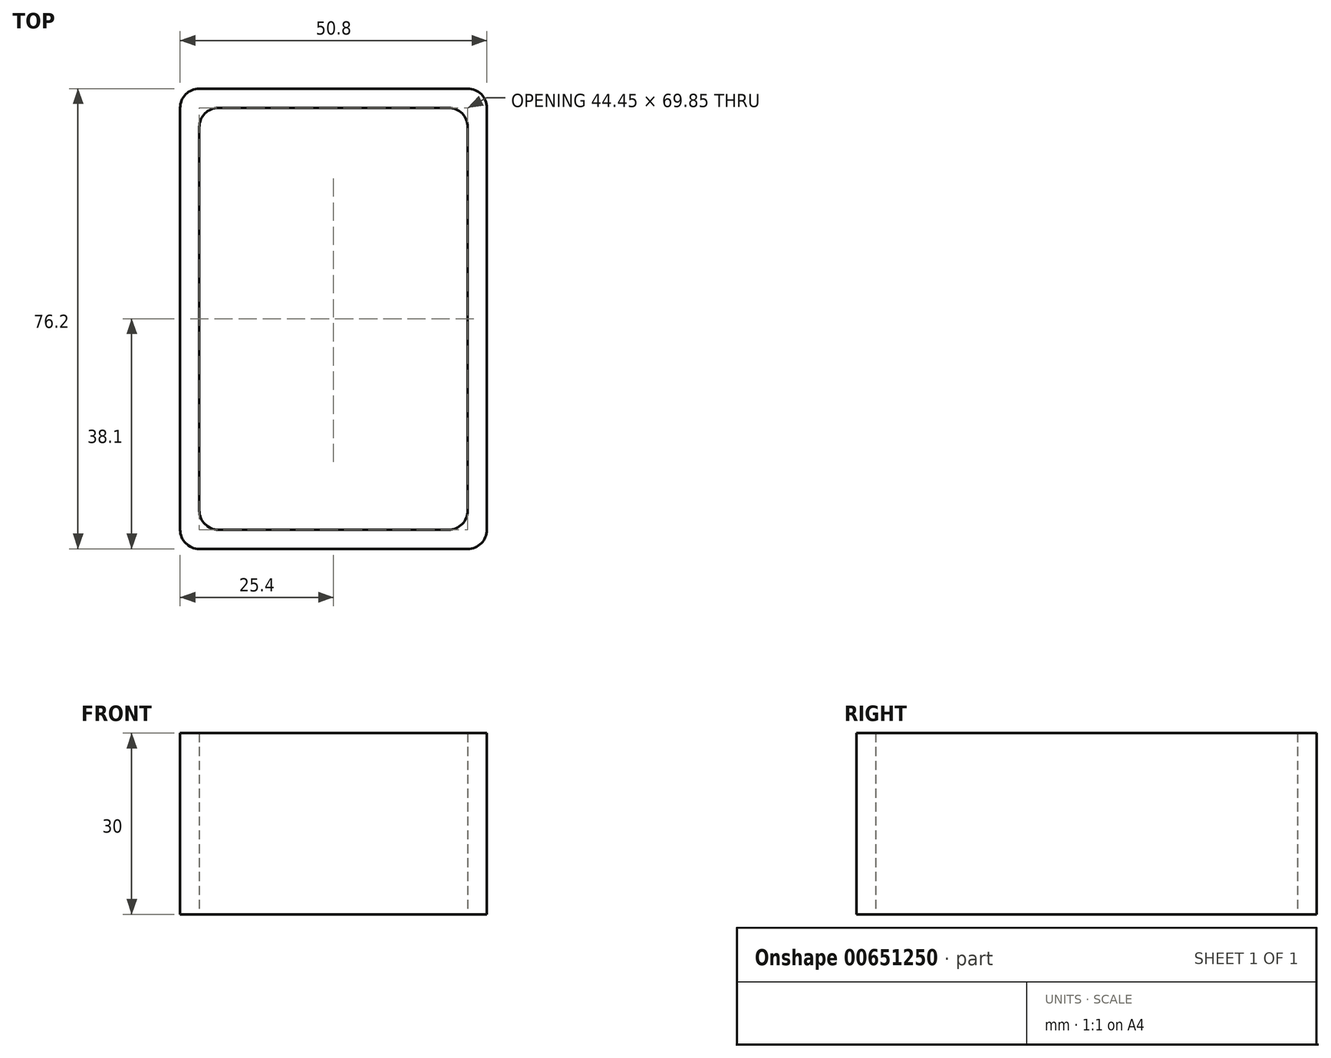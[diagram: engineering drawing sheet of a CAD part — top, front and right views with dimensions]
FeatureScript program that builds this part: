
annotation { "Feature Type Name" : "Feature", "Feature Type Description" : "" }
export const myFeature = defineFeature(function(context is Context, id is Id, definition is map)
    precondition{}
    {
        {
            var Q0;
            Q0=qCreatedBy(makeId("Top.planeOp"),FACE);
            var sketch = newSketch(context, id + "F0", { "sketchPlane" : qUnion([Q0])});
            skLineSegment(sketch, "E0.bottom", {"start": v(-25.4, 38.1) * mm, "end": v(25.4, 38.1) * mm});
            skLineSegment(sketch, "E0.top", {"start": v(-25.4, -38.1) * mm, "end": v(25.4, -38.1) * mm});
            skLineSegment(sketch, "E0.left", {"start": v(-25.4, 38.1) * mm, "end": v(-25.4, -38.1) * mm});
            skLineSegment(sketch, "E0.right", {"start": v(25.4, 38.1) * mm, "end": v(25.4, -38.1) * mm});
            skPoint(sketch, "E0.middle", {"position": v(0, 0) * mm});
            skLineSegment(sketch, "E1.bottom", {"start": v(-22.23, 34.93) * mm, "end": v(22.22, 34.93) * mm});
            skLineSegment(sketch, "E1.top", {"start": v(-22.23, -34.93) * mm, "end": v(22.22, -34.93) * mm});
            skLineSegment(sketch, "E1.left", {"start": v(-22.23, 34.93) * mm, "end": v(-22.23, -34.93) * mm});
            skLineSegment(sketch, "E1.right", {"start": v(22.22, 34.93) * mm, "end": v(22.22, -34.93) * mm});
            skSolve(sketch);
        }
        {
            assignVariable(context, id + "F1", {"name" : "Length", "anyValue" : 30});
        }
        {
            var Q0;
            Q0=makeQuery(id+"F0.imprint","IMPRINT",FACE,{"disambiguationData":[TD([[makeQuery(id+"F0.imprint","IMPRINT",EDGE,{"derivedFrom":sQuery(id+"F0.wireOp",EDGE,"E0.bottom")}),-1.0]])]});
            extrude(context, id + "F2", {"entities" : qUnion([Q0]), "depth" : (getVariable(context, 'Length')) * mm, "offsetDistance" : 25.4 * mm});
        }
        {
            var Q0;
            Q0=makeQuery(id+"F2.opExtrude","SWEPT_EDGE",EDGE,{"disambiguationData":[OSD([sQuery(id+"F0.wireOp",EDGE,"E1.bottom"),sQuery(id+"F0.wireOp",EDGE,"E1.left")])]});
            var Q1;
            Q1=makeQuery(id+"F2.opExtrude","SWEPT_EDGE",EDGE,{"disambiguationData":[OSD([sQuery(id+"F0.wireOp",EDGE,"E1.bottom"),sQuery(id+"F0.wireOp",EDGE,"E1.right")])]});
            var Q2;
            Q2=makeQuery(id+"F2.opExtrude","SWEPT_EDGE",EDGE,{"disambiguationData":[OSD([sQuery(id+"F0.wireOp",EDGE,"E1.top"),sQuery(id+"F0.wireOp",EDGE,"E1.right")])]});
            var Q3;
            Q3=makeQuery(id+"F2.opExtrude","SWEPT_EDGE",EDGE,{"disambiguationData":[OSD([sQuery(id+"F0.wireOp",EDGE,"E1.top"),sQuery(id+"F0.wireOp",EDGE,"E1.left")])]});
            var Q4;
            Q4=makeQuery(id+"F2.opExtrude","SWEPT_EDGE",EDGE,{"disambiguationData":[OSD([sQuery(id+"F0.wireOp",EDGE,"E0.bottom"),sQuery(id+"F0.wireOp",EDGE,"E0.right")])]});
            var Q5;
            Q5=makeQuery(id+"F2.opExtrude","SWEPT_EDGE",EDGE,{"disambiguationData":[OSD([sQuery(id+"F0.wireOp",EDGE,"E0.bottom"),sQuery(id+"F0.wireOp",EDGE,"E0.left")])]});
            var Q6;
            Q6=makeQuery(id+"F2.opExtrude","SWEPT_EDGE",EDGE,{"disambiguationData":[OSD([sQuery(id+"F0.wireOp",EDGE,"E0.top"),sQuery(id+"F0.wireOp",EDGE,"E0.right")])]});
            var Q7;
            Q7=makeQuery(id+"F2.opExtrude","SWEPT_EDGE",EDGE,{"disambiguationData":[OSD([sQuery(id+"F0.wireOp",EDGE,"E0.top"),sQuery(id+"F0.wireOp",EDGE,"E0.left")])]});
            fillet(context, id + "F3", {"entities" : qUnion([Q0, Q1, Q2, Q3, Q4, Q5, Q6, Q7]), "radius" : 3.17 * mm, "tangentPropagation" : true, "allowEdgeOverflow" : false});
        }
        {
            var Q0;
            Q0=makeQuery(id+"F2.opExtrude","SWEPT_FACE",FACE,{"disambiguationData":[OSD([sQuery(id+"F0.wireOp",EDGE,"E0.right")])]});
            var sketch = newSketch(context, id + "F4", { "sketchPlane" : qUnion([Q0])});
            skLineSegment(sketch, "E2", {"start": v(0, 381) * mm, "end": v(0, 228.6) * mm});
            skLineSegment(sketch, "E3.MirrorCS", {"start": v(0, 381) * mm, "end": v(0, 533.4) * mm});
            skPoint(sketch, "E4.middle", {"position": v(0, 228.6) * mm});
            skCircle(sketch, "E5", {"center": v(-16, 213.6) * mm, "radius": 3 * mm});
            skCircle(sketch, "E6", {"center": v(-16, 243.6) * mm, "radius": 3 * mm});
            skCircle(sketch, "E7", {"center": v(16, 243.6) * mm, "radius": 3 * mm});
            skCircle(sketch, "E8", {"center": v(16, 213.6) * mm, "radius": 3 * mm});
            skLineSegment(sketch, "E9", {"start": v(0, 381) * mm, "end": v(11.86, 381) * mm});
            skCircle(sketch, "E10.MirrorC", {"center": v(-16, 518.4) * mm, "radius": 3 * mm});
            skCircle(sketch, "E11.MirrorC", {"center": v(-16, 548.4) * mm, "radius": 3 * mm});
            skCircle(sketch, "E12.MirrorC", {"center": v(16, 548.4) * mm, "radius": 3 * mm});
            skCircle(sketch, "E13.MirrorC", {"center": v(16, 518.4) * mm, "radius": 3 * mm});
            skSolve(sketch);
        }
        {
            var Q0;
            Q0=makeQuery(id+"F4.imprint","IMPRINT",FACE,{"disambiguationData":[TD([[makeQuery(id+"F4.imprint","IMPRINT",EDGE,{"derivedFrom":sQuery(id+"F4.wireOp",EDGE,"E5")}),1.0]])]});
            var Q1;
            Q1=makeQuery(id+"F4.imprint","IMPRINT",FACE,{"disambiguationData":[TD([[makeQuery(id+"F4.imprint","IMPRINT",EDGE,{"derivedFrom":sQuery(id+"F4.wireOp",EDGE,"E6")}),1.0]])]});
            var Q2;
            Q2=makeQuery(id+"F4.imprint","IMPRINT",FACE,{"disambiguationData":[TD([[makeQuery(id+"F4.imprint","IMPRINT",EDGE,{"derivedFrom":sQuery(id+"F4.wireOp",EDGE,"E7")}),1.0]])]});
            var Q3;
            Q3=makeQuery(id+"F4.imprint","IMPRINT",FACE,{"disambiguationData":[TD([[makeQuery(id+"F4.imprint","IMPRINT",EDGE,{"derivedFrom":sQuery(id+"F4.wireOp",EDGE,"E8")}),1.0]])]});
            var Q4;
            Q4=makeQuery(id+"F4.imprint","IMPRINT",FACE,{"disambiguationData":[TD([[makeQuery(id+"F4.imprint","IMPRINT",EDGE,{"derivedFrom":sQuery(id+"F4.wireOp",EDGE,"E10.MirrorC")}),-1.0]])]});
            var Q5;
            Q5=makeQuery(id+"F4.imprint","IMPRINT",FACE,{"disambiguationData":[TD([[makeQuery(id+"F4.imprint","IMPRINT",EDGE,{"derivedFrom":sQuery(id+"F4.wireOp",EDGE,"E11.MirrorC")}),-1.0]])]});
            var Q6;
            Q6=makeQuery(id+"F4.imprint","IMPRINT",FACE,{"disambiguationData":[TD([[makeQuery(id+"F4.imprint","IMPRINT",EDGE,{"derivedFrom":sQuery(id+"F4.wireOp",EDGE,"E13.MirrorC")}),-1.0]])]});
            var Q7;
            Q7=makeQuery(id+"F4.imprint","IMPRINT",FACE,{"disambiguationData":[TD([[makeQuery(id+"F4.imprint","IMPRINT",EDGE,{"derivedFrom":sQuery(id+"F4.wireOp",EDGE,"E12.MirrorC")}),-1.0]])]});
            extrude(context, id + "F5", {"entities" : qUnion([Q0, Q1, Q2, Q3, Q4, Q5, Q6, Q7]), "operationType" : NewBodyOperationType.REMOVE, "endBound" : BoundingType.THROUGH_ALL, "oppositeDirection" : true, "depth" : 25.4 * mm, "offsetDistance" : 25.4 * mm});
        }
        {
            var Q0;
            Q0=makeQuery(id+"F2.opExtrude","SWEPT_FACE",FACE,{"disambiguationData":[OSD([sQuery(id+"F0.wireOp",EDGE,"E0.left")])]});
            var sketch = newSketch(context, id + "F6", { "sketchPlane" : qUnion([Q0])});
            skLineSegment(sketch, "E14.bottom", {"start": v(-34.92, 193.15) * mm, "end": v(34.93, 193.15) * mm});
            skLineSegment(sketch, "E14.top", {"start": v(-34.92, 572.65) * mm, "end": v(34.93, 572.65) * mm});
            skLineSegment(sketch, "E14.left", {"start": v(-34.92, 193.15) * mm, "end": v(-34.92, 572.65) * mm});
            skLineSegment(sketch, "E14.right", {"start": v(34.93, 193.15) * mm, "end": v(34.93, 572.65) * mm});
            skSolve(sketch);
        }
        {
            var Q0;
            Q0=makeQuery(id+"F6.imprint","IMPRINT",FACE,{"disambiguationData":[TD([[makeQuery(id+"F6.imprint","IMPRINT",EDGE,{"derivedFrom":sQuery(id+"F6.wireOp",EDGE,"E14.bottom")}),1.0]])]});
            extrude(context, id + "F7", {"entities" : qUnion([Q0]), "operationType" : NewBodyOperationType.REMOVE, "oppositeDirection" : true, "depth" : 25.4 * mm, "offsetDistance" : 25.4 * mm});
        }
    });
